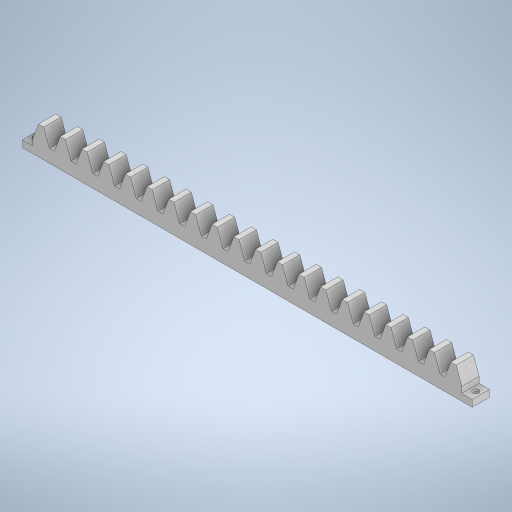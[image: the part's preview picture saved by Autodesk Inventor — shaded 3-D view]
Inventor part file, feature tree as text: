
AUTODESK INVENTOR PART (.ipt)
format: ipt  version: 2023.2 (Build 272271030, 271C)  size: 446,976 bytes
history: native  units: mm
features: projected_geometry x6, extrude x4, sketch x4
ambient origin geometry x8: Origin, YZ Plane, XZ Plane, XY Plane, X Axis, Y Axis, Z Axis, Center Point
bodies: Solid1 (feature_tree)
feature tree (14):
  extrude  "Extrusion1"  Depth=12.217305mm
  extrude  "Extrusion2"  Depth=10.0mm
  extrude  "Extrusion3"  Depth=18.862928mm
  extrude  "Extrusion4"  Depth=3.5mm
  sketch  "Sketch1"  dims[d3=30.0mm d4=12.217305mm]
  sketch  "Sketch2"  dims[d5=14.91mm d6=200.0mm d8=31.41mm d9=10.0mm d11=10.0mm]
  projected_geometry  "Projected Loop1"
  projected_geometry  "Projected Loop2"
  sketch  "Sketch3"  dims[d13=18.862928mm d14=620.799256mm d15=18.862928mm]
  projected_geometry  "Projected Loop3"
  projected_geometry  "Projected Loop4"
  sketch  "Sketch4"  dims[d16=18.862928mm d18=13.17215mm d19=13.17215mm d20=24.009256mm d21=22.5mm d22=23.944mm d23=3.010685mm d24=18.862928mm d25=25.0mm d26=0.0mm d27=15.0mm d28=25.0mm d29=15.0mm d30=25.0mm d31=10.0mm d32=0.0mm d33=5.3mm d34=0.0mm d35=0.0mm d36=8.7mm d37=3.5mm d38=0.0mm]
  projected_geometry  "Projected Loop5"
  projected_geometry  "Projected Loop6"
